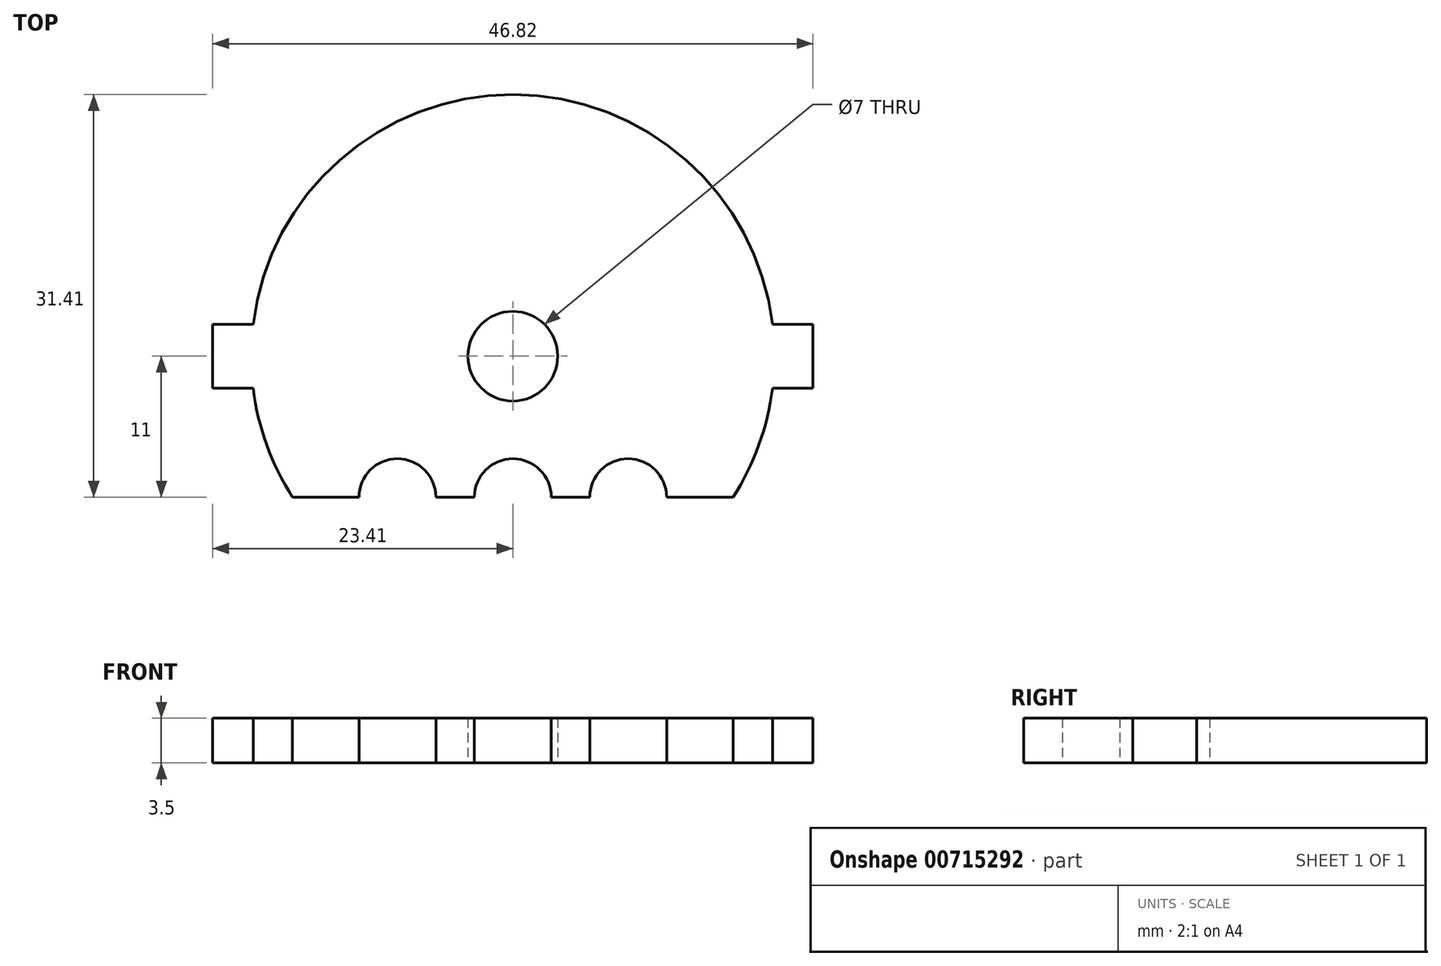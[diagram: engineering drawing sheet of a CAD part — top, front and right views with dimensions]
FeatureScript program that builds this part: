
annotation { "Feature Type Name" : "Feature", "Feature Type Description" : "" }
export const myFeature = defineFeature(function(context is Context, id is Id, definition is map)
    precondition{}
    {
        {
            var Q0;
            Q0=qCreatedBy(makeId("Top.planeOp"),FACE);
            var sketch = newSketch(context, id + "F0", { "sketchPlane" : qUnion([Q0])});
            skCircle(sketch, "E0", {"center": v(0, 0) * mm, "radius": 20.41 * mm});
            skLineSegment(sketch, "E1.bottom", {"start": v(-23.41, 2.5) * mm, "end": v(-17.41, 2.5) * mm});
            skLineSegment(sketch, "E1.top", {"start": v(-23.41, -2.5) * mm, "end": v(-17.41, -2.5) * mm});
            skLineSegment(sketch, "E1.left", {"start": v(-23.41, 2.5) * mm, "end": v(-23.41, -2.5) * mm});
            skLineSegment(sketch, "E1.right", {"start": v(-17.41, 2.5) * mm, "end": v(-17.41, -2.5) * mm});
            skPoint(sketch, "E1.middle", {"position": v(-20.41, 0) * mm});
            skLineSegment(sketch, "E2.MirrorCS", {"start": v(23.41, -2.5) * mm, "end": v(17.41, -2.5) * mm});
            skLineSegment(sketch, "E3.MirrorCS", {"start": v(23.41, 2.5) * mm, "end": v(23.41, -2.5) * mm});
            skLineSegment(sketch, "E4.MirrorCS", {"start": v(23.41, 2.5) * mm, "end": v(17.41, 2.5) * mm});
            skLineSegment(sketch, "E5.MirrorCS", {"start": v(17.41, 2.5) * mm, "end": v(17.41, -2.5) * mm});
            skCircle(sketch, "E6", {"center": v(0, 0) * mm, "radius": 3.5 * mm});
            skLineSegment(sketch, "E7", {"start": v(17.2, -11) * mm, "end": v(-38.36, -11) * mm});
            skPoint(sketch, "E8.orphan", {"position": v(0, -11) * mm});
            skCircle(sketch, "E9", {"center": v(0, -11) * mm, "radius": 3 * mm});
            skCircle(sketch, "E10", {"center": v(-9, -11) * mm, "radius": 3 * mm});
            skCircle(sketch, "E11.MirrorC", {"center": v(9, -11) * mm, "radius": 3 * mm});
            skSolve(sketch);
        }
        {
            var Q0;
            {var subQ4=sQuery(id+"F0.wireOp",EDGE,"E1.right");Q0=makeQuery(id+"F0.imprint","IMPRINT",FACE,{"disambiguationData":[TD([[makeQuery(id+"F0.imprint","IMPRINT",EDGE,{"derivedFrom":subQ4}),1.0]])]});}
            var Q1;
            {var subQ1=sQuery(id+"F0.wireOp",EDGE,"E7");var subQ5=sQuery(id+"F0.wireOp",EDGE,"E0");var subQ6=makeQuery(id+"F0.imprint","INTERSECT",VERTEX,{"disambiguationData":[OD(0.0)],"derivedFrom":[subQ5,subQ1]});Q1=makeQuery(id+"F0.imprint","IMPRINT",FACE,{"disambiguationData":[TD([[makeQuery(id+"F0.imprint","IMPRINT",EDGE,{"disambiguationData":[TD([[subQ6,1.0]])],"derivedFrom":subQ5}),1.0]])]});}
            var Q2;
            {var subQ5=sQuery(id+"F0.wireOp",EDGE,"E1.right");Q2=makeQuery(id+"F0.imprint","IMPRINT",FACE,{"disambiguationData":[TD([[makeQuery(id+"F0.imprint","IMPRINT",EDGE,{"derivedFrom":subQ5}),-1.0]])]});}
            var Q3;
            {var subQ5=sQuery(id+"F0.wireOp",EDGE,"E1.left");Q3=makeQuery(id+"F0.imprint","IMPRINT",FACE,{"disambiguationData":[TD([[makeQuery(id+"F0.imprint","IMPRINT",EDGE,{"derivedFrom":subQ5}),1.0]])]});}
            var Q4;
            {var subQ5=sQuery(id+"F0.wireOp",EDGE,"E5.MirrorCS");Q4=makeQuery(id+"F0.imprint","IMPRINT",FACE,{"disambiguationData":[TD([[makeQuery(id+"F0.imprint","IMPRINT",EDGE,{"derivedFrom":subQ5}),1.0]])]});}
            var Q5;
            {var subQ5=sQuery(id+"F0.wireOp",EDGE,"E3.MirrorCS");Q5=makeQuery(id+"F0.imprint","IMPRINT",FACE,{"disambiguationData":[TD([[makeQuery(id+"F0.imprint","IMPRINT",EDGE,{"derivedFrom":subQ5}),-1.0]])]});}
            extrude(context, id + "F1", {"entities" : qUnion([Q0, Q1, Q2, Q3, Q4, Q5]), "depth" : 3.5 * mm, "offsetDistance" : 25 * mm});
        }
    });
